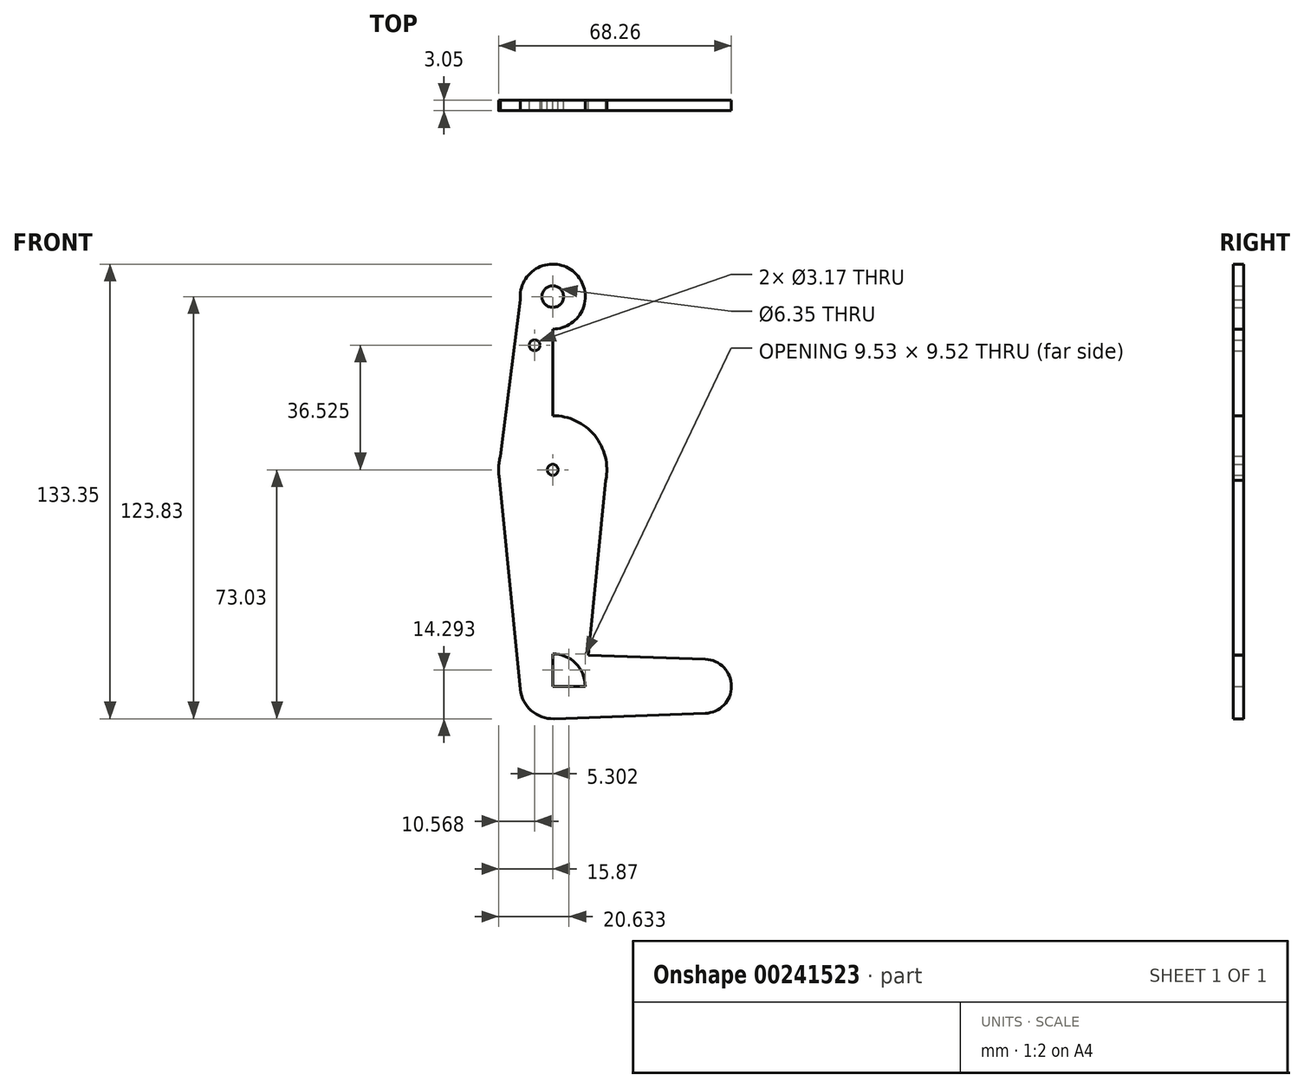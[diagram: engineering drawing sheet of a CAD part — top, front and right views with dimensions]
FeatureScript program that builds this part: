
annotation { "Feature Type Name" : "Feature", "Feature Type Description" : "" }
export const myFeature = defineFeature(function(context is Context, id is Id, definition is map)
    precondition{}
    {
        {
            var Q0;
            Q0=qCreatedBy(makeId("Front.planeOp"),FACE);
            var sketch = newSketch(context, id + "F0", { "sketchPlane" : qUnion([Q0])});
            skLineSegment(sketch, "E0", {"start": v(0, 0) * mm, "end": v(0, 50.8) * mm});
            skLineSegment(sketch, "E1", {"start": v(0, 0) * mm, "end": v(0, -63.5) * mm});
            skLineSegment(sketch, "E2", {"start": v(0, -63.5) * mm, "end": v(44.45, -63.5) * mm});
            skCircle(sketch, "E3", {"center": v(0, 50.8) * mm, "radius": 9.53 * mm});
            skCircle(sketch, "E4", {"center": v(44.45, -63.5) * mm, "radius": 7.94 * mm});
            skCircle(sketch, "E5", {"center": v(0, -63.5) * mm, "radius": 9.53 * mm});
            skCircle(sketch, "E6", {"center": v(0, 0) * mm, "radius": 15.88 * mm});
            skLineSegment(sketch, "E7", {"start": v(44.77, -71.43) * mm, "end": v(0, -73.03) * mm});
            skLineSegment(sketch, "E8", {"start": v(0, -53.97) * mm, "end": v(44.73, -55.57) * mm});
            skLineSegment(sketch, "E9", {"start": v(-15.88, 0) * mm, "end": v(-9.48, -64.44) * mm});
            skLineSegment(sketch, "E10", {"start": v(15.88, 0) * mm, "end": v(9.57, -63.5) * mm});
            skLineSegment(sketch, "E11", {"start": v(-9.48, 49.86) * mm, "end": v(-15.88, 0) * mm});
            skLineSegment(sketch, "E12", {"start": v(9.57, 51.03) * mm, "end": v(15.88, 1.39) * mm});
            skCircle(sketch, "E13", {"center": v(0, 50.8) * mm, "radius": 3.18 * mm});
            skCircle(sketch, "E14", {"center": v(-5.3, 36.53) * mm, "radius": 1.59 * mm});
            skCircle(sketch, "E15", {"center": v(0, 0) * mm, "radius": 1.59 * mm});
            skSolve(sketch);
        }
        {
            var Q0;
            Q0 = qSketchRegion(id + "F0", true);
            extrude(context, id + "F1", {"entities" : qUnion([Q0]), "depth" : 3.05 * mm});
        }
    });
